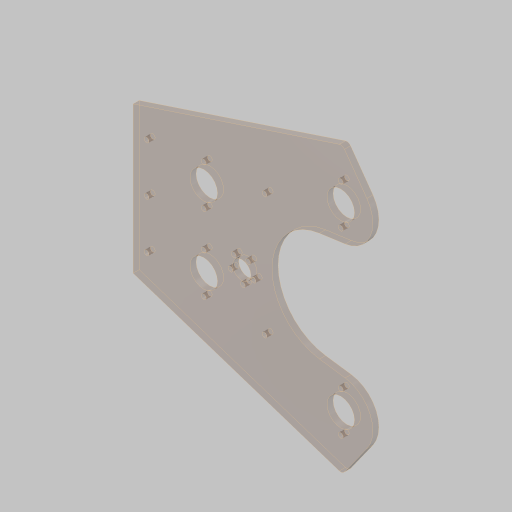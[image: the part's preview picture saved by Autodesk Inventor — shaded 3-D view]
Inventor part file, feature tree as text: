
AUTODESK INVENTOR PART (.ipt)
format: ipt  version: 2023.5 (Build 275446000, 446)  size: 184,320 bytes
history: native  units: in
note: dims shown in document units (in); Inventor stores cm internally (conversion verified against a paired STEP export)
features: sketch x1, extrude x1, hole x1
ambient origin geometry x8: Origin, YZ Plane, XZ Plane, XY Plane, X Axis, Y Axis, Z Axis, Center Point
bodies: Solid1 (feature_tree)
feature tree (3):
  sketch  "Sketch1"  dims[d0=3.0in d1=3.0in d2=4.5in d4=7.3485in d5=1.125in d6=0.75in d7=1.128in d8=1.88in d9=3.125in d10=5.6076in d11=5.992in d12=1.125in d13=0.4688in d14=0.75in d15=1.0in d16=1.9685in d18=360.0deg d20=0.1875in d21=1.5in d22=1.0in d23=6.0in d24=8.5in d25=60.0deg d26=5.0in d27=0.25in d28=0.0in d29=0.375in d30=0.25in d32=1.655in d33=1.655in d34=1.655in d35=1.655in d36=0.75in d37=0.201in d38=0.75in d39=0.385in d40=0.25in d41=0.5635in d42=1.0in d43=0.8108in d44=4.0in]
  extrude  "Extrusion1"  Depth=0.25in
  hole  "Hole1"  [1 undecoded]
note: 1 required parameter value undecoded (feature->parameter linkage not recoverable at this tier; creation-order binding heuristic only, values carry confidence <= 0.55)
